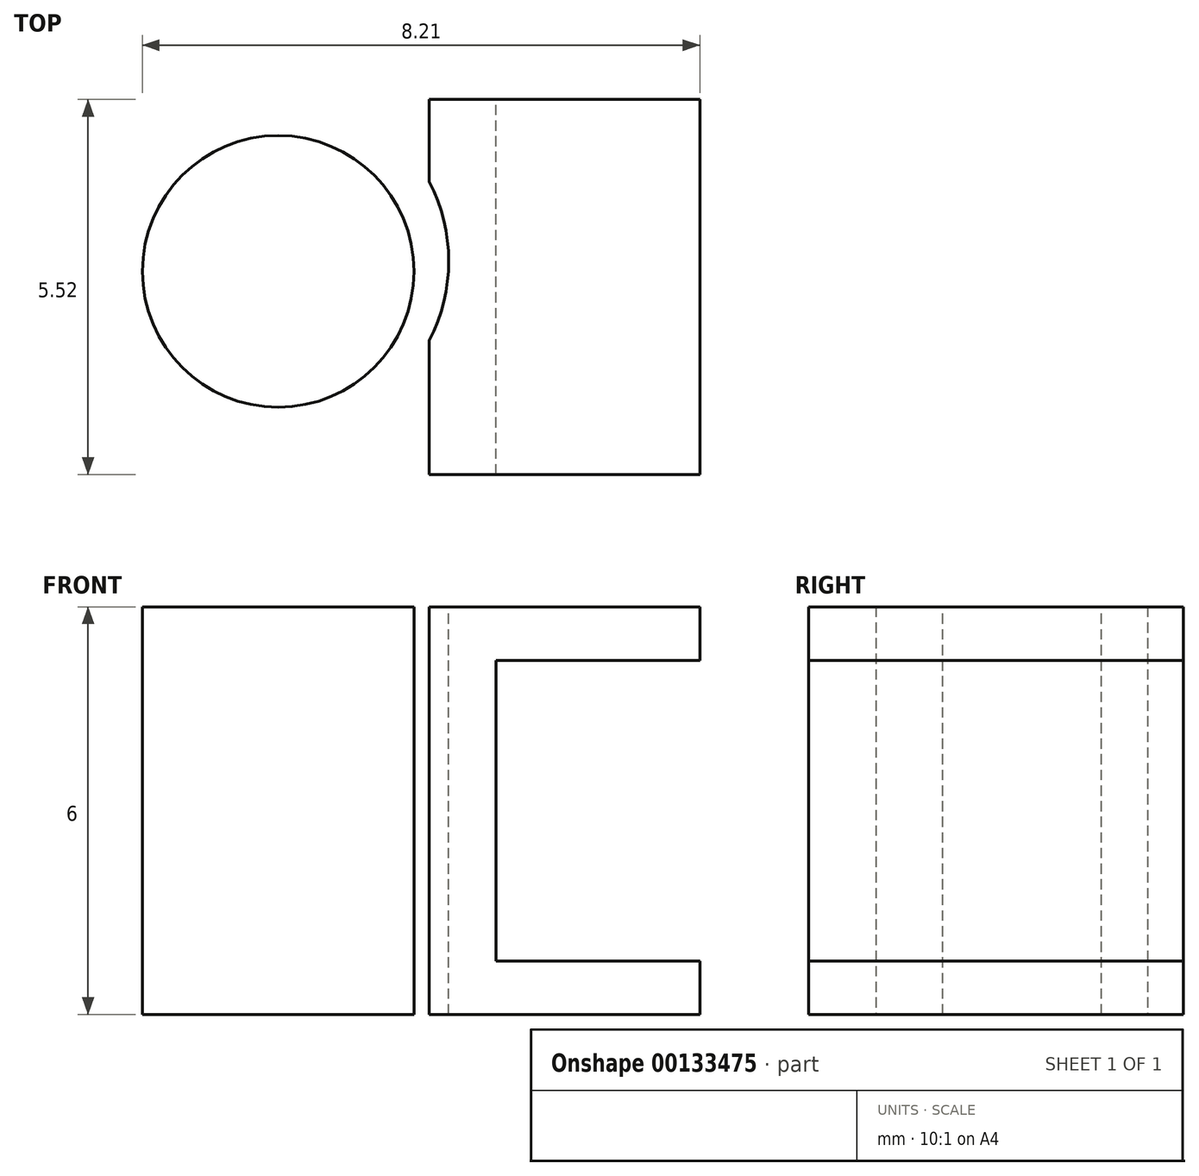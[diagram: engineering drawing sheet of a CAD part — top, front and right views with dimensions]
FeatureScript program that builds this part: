
annotation { "Feature Type Name" : "Feature", "Feature Type Description" : "" }
export const myFeature = defineFeature(function(context is Context, id is Id, definition is map)
    precondition{}
    {
        {
            var Q0;
            Q0=qCreatedBy(makeId("Top.planeOp"),FACE);
            var sketch = newSketch(context, id + "F0", { "sketchPlane" : qUnion([Q0])});
            skCircle(sketch, "E0", {"center": v(0, 0) * mm, "radius": 2 * mm});
            skLineSegment(sketch, "E1.bottom", {"start": v(2.22, 2.53) * mm, "end": v(6.2, 2.53) * mm});
            skLineSegment(sketch, "E1.top", {"start": v(2.22, -2.99) * mm, "end": v(6.2, -2.99) * mm});
            skLineSegment(sketch, "E1.left", {"start": v(2.22, 2.53) * mm, "end": v(2.22, -2.99) * mm});
            skLineSegment(sketch, "E1.right", {"start": v(6.2, 2.53) * mm, "end": v(6.2, -2.99) * mm});
            skSolve(sketch);
        }
        {
            var Q0;
            Q0=makeQuery(id+"F0.imprint","IMPRINT",FACE,{"disambiguationData":[TD([[makeQuery(id+"F0.imprint","IMPRINT",EDGE,{"derivedFrom":sQuery(id+"F0.wireOp",EDGE,"E1.bottom")}),-1.0]])]});
            var Q1;
            Q1=makeQuery(id+"F0.imprint","IMPRINT",FACE,{"disambiguationData":[TD([[makeQuery(id+"F0.imprint","IMPRINT",EDGE,{"derivedFrom":sQuery(id+"F0.wireOp",EDGE,"E0")}),1.0]])]});
            extrude(context, id + "F1", {"entities" : qUnion([Q0, Q1]), "depth" : 6 * mm});
        }
        {
            var Q0;
            Q0=makeQuery(id+"F1.opExtrude","CAP_FACE",FACE,{"disambiguationData":[OSD([sQuery(id+"F0.wireOp",EDGE,"E0")])],"isStart":false});
            var sketch = newSketch(context, id + "F2", { "sketchPlane" : qUnion([Q0])});
            skCircle(sketch, "E2", {"center": v(0, 0.15) * mm, "radius": 2.51 * mm});
            skSolve(sketch);
        }
        {
            var Q0;
            Q0=makeQuery(id+"F2.imprint","IMPRINT",FACE,{"disambiguationData":[TD([[makeQuery(id+"F2.imprint","IMPRINT",EDGE,{"derivedFrom":sQuery(id+"F2.wireOp",EDGE,"E2")}),1.0]])]});
            extrude(context, id + "F3", {"entities" : qUnion([Q0]), "operationType" : NewBodyOperationType.REMOVE, "oppositeDirection" : true, "depth" : 20 * mm});
        }
        {
            var Q0;
            Q0=makeQuery(id+"F1.opExtrude","SWEPT_FACE",FACE,{"disambiguationData":[OSD([sQuery(id+"F0.wireOp",EDGE,"E1.right")])]});
            var sketch = newSketch(context, id + "F4", { "sketchPlane" : qUnion([Q0])});
            skLineSegment(sketch, "E3.bottom", {"start": v(-4.58, 5.21) * mm, "end": v(4.07, 5.21) * mm});
            skLineSegment(sketch, "E3.top", {"start": v(-4.58, 0.79) * mm, "end": v(4.07, 0.79) * mm});
            skLineSegment(sketch, "E3.left", {"start": v(-4.58, 5.21) * mm, "end": v(-4.58, 0.79) * mm});
            skLineSegment(sketch, "E3.right", {"start": v(4.07, 5.21) * mm, "end": v(4.07, 0.79) * mm});
            skSolve(sketch);
        }
        {
            var Q0;
            {var subQ0=sQuery(id+"F4.wireOp",EDGE,"E3.bottom");var subQ1=sQuery(id+"F0.wireOp",EDGE,"E1.right");var subQ2=makeQuery(id+"F1.opExtrude","SWEPT_EDGE",EDGE,{"disambiguationData":[OSD([sQuery(id+"F0.wireOp",EDGE,"E1.top"),subQ1])]});var subQ3=makeQuery(id+"F4.imprint","INTERSECT",VERTEX,{"derivedFrom":[subQ2,subQ0]});Q0=makeQuery(id+"F4.imprint","IMPRINT",FACE,{"disambiguationData":[TD([[makeQuery(id+"F4.imprint","IMPRINT",EDGE,{"disambiguationData":[TD([[subQ3,-1.0]])],"derivedFrom":subQ0}),-1.0]])]});}
            extrude(context, id + "F5", {"entities" : qUnion([Q0]), "operationType" : NewBodyOperationType.REMOVE, "oppositeDirection" : true, "depth" : 3 * mm});
        }
    });
